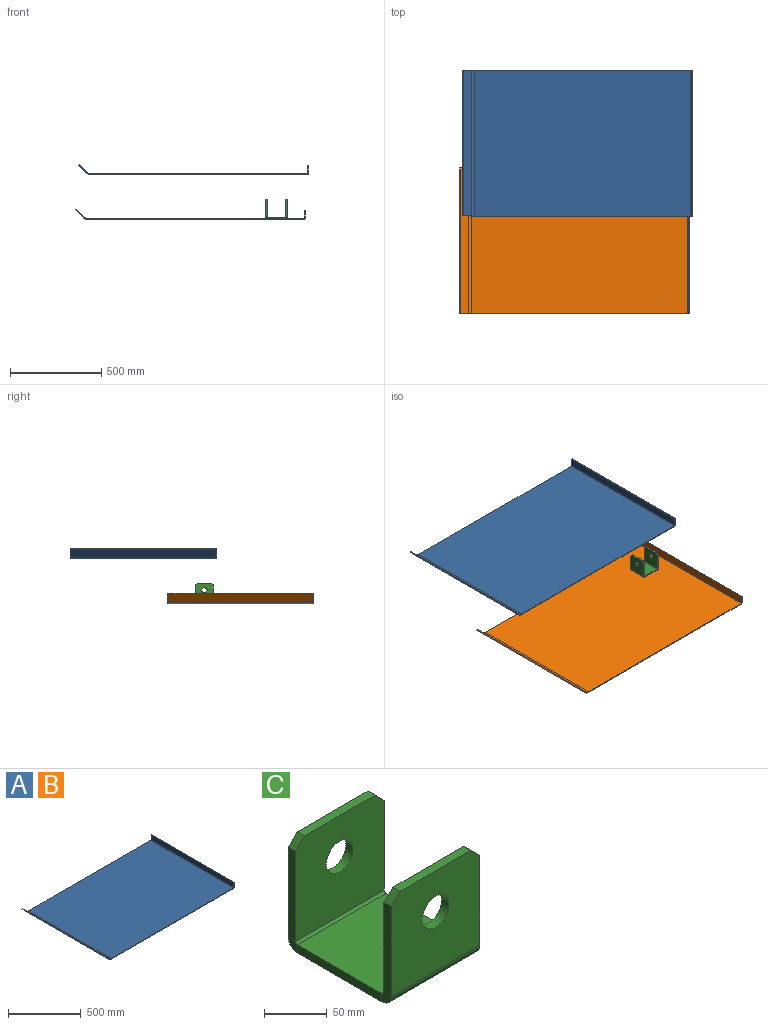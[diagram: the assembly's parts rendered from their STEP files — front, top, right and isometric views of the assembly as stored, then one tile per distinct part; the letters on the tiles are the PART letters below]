
ASSEMBLY  parts=3 mates=1
PART A: 22 faces, bbox 1260.1x800x56.6 mm
  f0: plane 1187.34x5mm, normal (0,-1,0), area 5936.7mm2, adj f2,f3,f9,f19
  f1: plane 1187.34x5mm, normal (0,1,0), area 5936.7mm2, adj f2,f3,f10,f18
  f2: plane 1187.34x800mm, normal (0,0,-1), area 949875.7mm2, adj f0,f1,f11,f20
  f3: plane 1187.34x800mm, normal (0,0,1), area 949875.7mm2, adj f0,f1,f12,f21
  f4: plane 42.7x5mm, normal (0,-1,0), area 213.5mm2, adj f6,f7,f8,f9
  f5: plane 42.7x5mm, normal (0,1,0), area 213.5mm2, adj f6,f7,f8,f10
  f6: plane 800x5mm, normal (0,0,1), area 4000mm2, adj f4,f5,f7,f8
  f7: plane 800x42.7mm, normal (1,0,0), area 34160mm2, adj f4,f5,f6,f11
  f8: plane 800x42.7mm, normal (-1,0,0), area 34160mm2, adj f4,f5,f6,f12
  f9: plane 7.3x7.3mm, normal (0,-1,0), area 37.7mm2, adj f0,f4,f11,f12
  f10: plane 7.3x7.3mm, normal (0,1,0), area 37.7mm2, adj f1,f5,f11,f12
  f11: cylinder r=7.3mm len=800mm, axis (0,-1,0), area 9173.5mm2, adj f2,f7,f9,f10
  f12: cylinder r=2.3mm len=800mm, axis (0,-1,0), area 2890.3mm2, adj f3,f8,f9,f10
  f13: plane 47.78x47.78mm, normal (0,1,0), area 312.9mm2, adj f15,f16,f17,f18
  f14: plane 47.78x47.78mm, normal (0,-1,0), area 312.9mm2, adj f15,f16,f17,f19
  f15: plane 800x3.54mm, normal (-0.71,0,0.71), area 4000mm2, adj f13,f14,f16,f17
  f16: plane 800x44.25mm, normal (-0.71,0,-0.71), area 50058.9mm2, adj f13,f14,f15,f20
  f17: plane 800x44.25mm, normal (0.71,0,0.71), area 50058.9mm2, adj f13,f14,f15,f21
  f18: plane 21.21x12.32mm, normal (0,1,0), area 108mm2, adj f1,f13,f20,f21
  f19: plane 21.21x12.32mm, normal (0,-1,0), area 108mm2, adj f0,f14,f20,f21
  f20: cylinder r=30mm len=800mm, axis (0,1,0), area 18849.6mm2, adj f2,f16,f18,f19
  f21: cylinder r=25mm len=800mm, axis (0,1,0), area 15708mm2, adj f3,f17,f18,f19
PART B: same geometry as A
PART C: 28 faces, bbox 100x116x108 mm
  f0: plane 95.4x8mm, normal (-1,0,0), area 763.2mm2, adj f2,f3,f12,f23
  f1: plane 95.4x8mm, normal (1,0,0), area 763.2mm2, adj f2,f3,f11,f22
  f2: plane 100x95.4mm, normal (0,0,-1), area 9540mm2, adj f0,f1,f13,f24
  f3: plane 100x95.4mm, normal (0,0,1), area 9540mm2, adj f0,f1,f14,f25
  f4: plane 87.7x8mm, normal (-1,0,0), area 701.6mm2, adj f8,f9,f10,f12
  f5: plane 87.7x8mm, normal (1,0,0), area 701.6mm2, adj f6,f9,f10,f11
  f6: plane 10x10mm, normal (0.71,0,0.71), area 113.1mm2, adj f5,f7,f9,f10
  f7: plane 80x8mm, normal (0,0,1), area 640mm2, adj f6,f8,f9,f10
  f8: plane 10x10mm, normal (-0.71,0,0.71), area 113.1mm2, adj f4,f7,f9,f10
  f9: plane 100x97.7mm, normal (0,-1,0), area 8963.1mm2, adj f4,f5,f6,f7,f8,f13,f27
  f10: plane 100x97.7mm, normal (0,1,0), area 8963.1mm2, adj f4,f5,f6,f7,f8,f14,f27
  f11: plane 10.3x10.3mm, normal (1,0,0), area 79.2mm2, adj f1,f5,f13,f14
  f12: plane 10.3x10.3mm, normal (-1,0,0), area 79.2mm2, adj f0,f4,f13,f14
  f13: cylinder r=10.3mm len=100mm, axis (1,0,0), area 1617.9mm2, adj f2,f9,f11,f12
  f14: cylinder r=2.3mm len=100mm, axis (1,0,0), area 361.3mm2, adj f3,f10,f11,f12
  f15: plane 80x8mm, normal (0,0,1), area 640mm2, adj f16,f19,f20,f21
  f16: plane 10x10mm, normal (0.71,0,0.71), area 113.1mm2, adj f15,f17,f20,f21
  f17: plane 87.7x8mm, normal (1,0,0), area 701.6mm2, adj f16,f20,f21,f22
  f18: plane 87.7x8mm, normal (-1,0,0), area 701.6mm2, adj f19,f20,f21,f23
  f19: plane 10x10mm, normal (-0.71,0,0.71), area 113.1mm2, adj f15,f18,f20,f21
  f20: plane 100x97.7mm, normal (0,1,0), area 8963.1mm2, adj f15,f16,f17,f18,f19,f24,f26
  f21: plane 100x97.7mm, normal (0,-1,0), area 8963.1mm2, adj f15,f16,f17,f18,f19,f25,f26
  f22: plane 10.3x10.3mm, normal (1,0,0), area 79.2mm2, adj f1,f17,f24,f25
  f23: plane 10.3x10.3mm, normal (-1,0,0), area 79.2mm2, adj f0,f18,f24,f25
  f24: cylinder r=10.3mm len=100mm, axis (1,0,0), area 1617.9mm2, adj f2,f20,f22,f23
  f25: cylinder r=2.3mm len=100mm, axis (1,0,0), area 361.3mm2, adj f3,f21,f22,f23
  f26: cylinder r=15mm len=30mm, axis (0,-1,0), area 754mm2, adj f20,f21
  f27: cylinder r=15mm len=30mm, axis (0,-1,0), area 754mm2, adj f9,f10
PLACE A t=(-268.71,191.89,69.45)mm
PLACE B t=(-286.31,-344.14,-177.14)mm
PLACE C rot(axis=(0,0,-1),90deg) t=(544.84,62.87,-164.14)mm
MATE fastened C.f2 <-> B.f3  axis (0,0,-1) through (494.84,83.61,-172.14)mm
